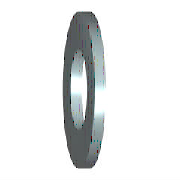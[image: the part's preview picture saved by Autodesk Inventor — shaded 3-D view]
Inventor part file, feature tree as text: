
AUTODESK INVENTOR PART (.ipt)
format: ipt  version: 2016 (Build 200138000, 138)  size: 110,592 bytes
history: native  units: mm (DEFAULTED — no unit token found)
features: other x1, plane x1, sketch x1
ambient origin geometry x7: Origin, YZ Plane, XY Plane, X Axis, Y Axis, Z Axis, Center Point
bodies: Solid1 (feature_tree), Body (feature_tree)
feature tree (3):
  other  "Work Axis1"
  plane  "Work Plane1"
  sketch  "Sketch"  dims[d0=4.3mm d1=9.0mm d2=0.8mm d3=0.0mm d4=0.0mm d5=0.0mm d6=0.0mm d7=0.0mm]
